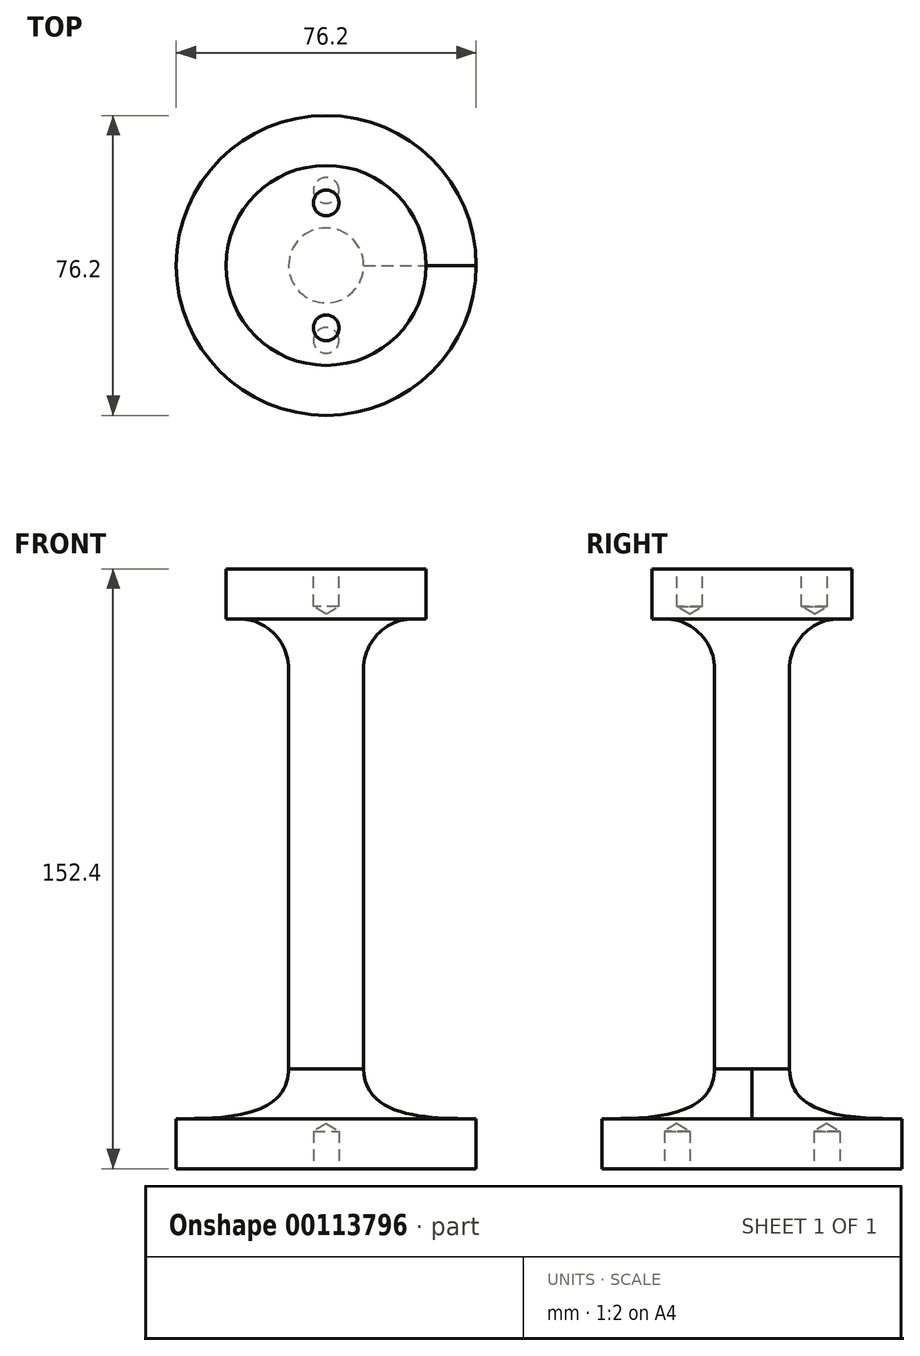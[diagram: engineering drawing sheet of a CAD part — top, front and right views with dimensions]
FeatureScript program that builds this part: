
annotation { "Feature Type Name" : "Feature", "Feature Type Description" : "" }
export const myFeature = defineFeature(function(context is Context, id is Id, definition is map)
    precondition{}
    {
        {
            var Q0;
            Q0=qCreatedBy(makeId("Front.planeOp"),FACE);
            var sketch = newSketch(context, id + "F0", { "sketchPlane" : qUnion([Q0])});
            skLineSegment(sketch, "E0", {"start": v(-82.45, 106.88) * mm, "end": v(-82.45, -45.52) * mm});
            skLineSegment(sketch, "E1.0", {"start": v(-60.23, 94.18) * mm, "end": v(-57.05, 94.18) * mm});
            skLineSegment(sketch, "E2.0", {"start": v(-55.73, -32.82) * mm, "end": v(-44.35, -32.82) * mm});
            skLineSegment(sketch, "E3.trimOffspring", {"start": v(-72.93, 81.48) * mm, "end": v(-72.93, -32.82) * mm});
            skLineSegment(sketch, "E4", {"start": v(-57.05, 94.18) * mm, "end": v(-57.05, 106.88) * mm});
            skLineSegment(sketch, "E5", {"start": v(-44.35, -45.52) * mm, "end": v(-44.35, -32.82) * mm});
            skLineSegment(sketch, "E6", {"start": v(-82.45, 106.88) * mm, "end": v(-57.05, 106.88) * mm});
            skLineSegment(sketch, "E7", {"start": v(-82.45, -45.52) * mm, "end": v(-44.35, -45.52) * mm});
            skPoint(sketch, "E8.visualSharp", {"position": v(-72.93, 94.18) * mm});
            skArc(sketch, "E8.filletArc", {"start": v(-60.23, 94.18) * mm, "mid": v(-69.2, 90.46) * mm, "end": v(-72.93, 81.48) * mm});
            skFitSpline(sketch, "E9", {"points": [v(-72.93, -20.12) * mm, v(-44.35, -32.82) * mm], "startDerivative": vector(0, -38.1) * mm, "endDerivative": vector(34.12, 0) * mm});
            skSolve(sketch);
        }
        {
            var Q0;
            Q0 = qSketchRegion(id + "F0", true);
            var Q1;
            Q1=sQuery(id+"F0.wireOp",EDGE,"E0");
            revolve(context, id + "F1", {"entities" : qUnion([Q0]), "axis" : qUnion([Q1]), "revolveType" : RevolveType.FULL});
        }
        {
            var Q0;
            Q0=makeQuery(id+"F1.opRevolve","SWEPT_FACE",FACE,{"disambiguationData":[OSD([sQuery(id+"F0.wireOp",EDGE,"E6")])]});
            var sketch = newSketch(context, id + "F2", { "sketchPlane" : qUnion([Q0])});
            skCircle(sketch, "E10", {"center": v(-82.45, 0) * mm, "radius": 15.87 * mm, "construction": true});
            skPoint(sketch, "E11", {"position": v(-82.45, 15.87) * mm});
            skPoint(sketch, "E12", {"position": v(-82.45, -15.87) * mm});
            skSolve(sketch);
        }
        {
            var Q0;
            Q0=sQuery(id+"F2.wireOp",VERTEX,"E11");
            var Q1;
            Q1=sQuery(id+"F2.wireOp",VERTEX,"E12");
            var Q2;
            Q2=makeQuery(id+"F1.opRevolve","SWEPT_BODY",BODY,{"disambiguationData":[OSD([sQuery(id+"F0.wireOp",EDGE,"E0"),sQuery(id+"F0.wireOp",EDGE,"E1.0"),sQuery(id+"F0.wireOp",EDGE,"E3.trimOffspring"),sQuery(id+"F0.wireOp",EDGE,"E4"),sQuery(id+"F0.wireOp",EDGE,"E5"),sQuery(id+"F0.wireOp",EDGE,"E6"),sQuery(id+"F0.wireOp",EDGE,"E7"),sQuery(id+"F0.wireOp",EDGE,"E8.filletArc"),sQuery(id+"F0.wireOp",EDGE,"E9")])]});
            hole(context, id + "F3", {"style" : HoleStyle.SIMPLE, "endStyle" : HoleEndStyle.BLIND, "standardTappedOrClearance" : lookupTablePath({ "standard" : "ANSI", "fit" : "Close", "size" : "1/4", "type" : "Clearance" }), "standardBlindInLast" : lookupTablePath({ "fit" : "Close", "standard" : "ANSI", "size" : "1/4", "type" : "Clearance" }), "holeDiameter" : 6.53 * mm, "holeDepth" : 9.52 * mm, "locations" : qUnion([Q0, Q1]), "scope" : qUnion([Q2])});
        }
        {
            var Q0;
            Q0=makeQuery(id+"F1.opRevolve","SWEPT_FACE",FACE,{"disambiguationData":[OSD([sQuery(id+"F0.wireOp",EDGE,"E7")])]});
            var sketch = newSketch(context, id + "F4", { "sketchPlane" : qUnion([Q0])});
            skCircle(sketch, "E13", {"center": v(-82.45, 0) * mm, "radius": 19.05 * mm, "construction": true});
            skPoint(sketch, "E14", {"position": v(-82.45, 19.05) * mm});
            skPoint(sketch, "E15", {"position": v(-82.45, -19.05) * mm});
            skSolve(sketch);
        }
        {
            var Q0;
            Q0=sQuery(id+"F4.wireOp",VERTEX,"E14");
            var Q1;
            Q1=sQuery(id+"F4.wireOp",VERTEX,"E15");
            var Q2;
            Q2=makeQuery(id+"F1.opRevolve","SWEPT_BODY",BODY,{"disambiguationData":[OSD([sQuery(id+"F0.wireOp",EDGE,"E0"),sQuery(id+"F0.wireOp",EDGE,"E1.0"),sQuery(id+"F0.wireOp",EDGE,"E3.trimOffspring"),sQuery(id+"F0.wireOp",EDGE,"E4"),sQuery(id+"F0.wireOp",EDGE,"E5"),sQuery(id+"F0.wireOp",EDGE,"E6"),sQuery(id+"F0.wireOp",EDGE,"E7"),sQuery(id+"F0.wireOp",EDGE,"E8.filletArc"),sQuery(id+"F0.wireOp",EDGE,"E9")])]});
            hole(context, id + "F5", {"style" : HoleStyle.SIMPLE, "endStyle" : HoleEndStyle.BLIND, "standardTappedOrClearance" : lookupTablePath({ "standard" : "ANSI", "fit" : "Close", "size" : "1/4", "type" : "Clearance" }), "standardBlindInLast" : lookupTablePath({ "fit" : "Close", "standard" : "ANSI", "size" : "1/4", "type" : "Clearance" }), "holeDiameter" : 6.53 * mm, "holeDepth" : 9.52 * mm, "locations" : qUnion([Q0, Q1]), "scope" : qUnion([Q2])});
        }
    });
